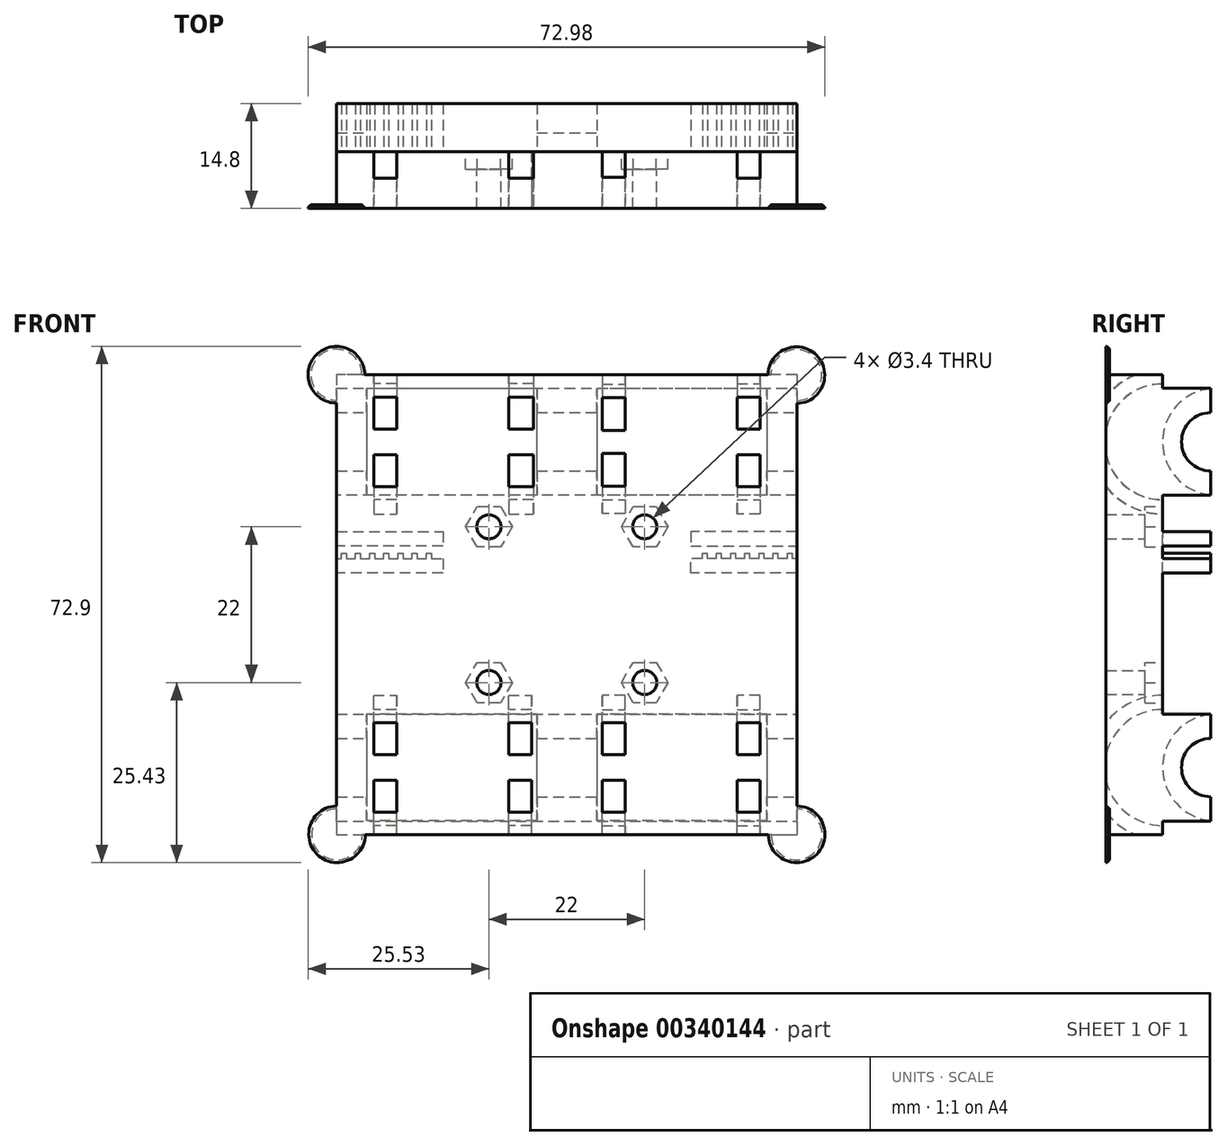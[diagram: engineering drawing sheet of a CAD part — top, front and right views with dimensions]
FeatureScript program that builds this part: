
annotation { "Feature Type Name" : "Feature", "Feature Type Description" : "" }
export const myFeature = defineFeature(function(context is Context, id is Id, definition is map)
    precondition{}
    {
        {
            var Q0;
            Q0=qCreatedBy(makeId("Front.planeOp"),FACE);
            var sketch = newSketch(context, id + "F0", { "sketchPlane" : qUnion([Q0])});
            skLineSegment(sketch, "E0", {"start": v(32.5, 32.5) * mm, "end": v(-32.5, 32.5) * mm});
            skLineSegment(sketch, "E1", {"start": v(-32.5, 32.5) * mm, "end": v(-32.5, -32.5) * mm});
            skLineSegment(sketch, "E2", {"start": v(-32.5, -32.5) * mm, "end": v(32.5, -32.5) * mm});
            skLineSegment(sketch, "E3", {"start": v(32.5, 32.5) * mm, "end": v(32.5, -32.5) * mm});
            skSolve(sketch);
        }
        {
            var Q0;
            Q0=makeQuery(id+"F0.imprint","IMPRINT",FACE,{"disambiguationData":[TD([[makeQuery(id+"F0.imprint","IMPRINT",EDGE,{"derivedFrom":sQuery(id+"F0.wireOp",EDGE,"E0")}),1.0]])]});
            extrude(context, id + "F1", {"entities" : qUnion([Q0]), "depth" : 8 * mm});
        }
        {
            var Q0;
            Q0=qCreatedBy(makeId("Front.planeOp"),FACE);
            var sketch = newSketch(context, id + "F2", { "sketchPlane" : qUnion([Q0])});
            skLineSegment(sketch, "E4", {"start": v(0, 0) * mm, "end": v(-11, 0) * mm});
            skLineSegment(sketch, "E5", {"start": v(-11, 0) * mm, "end": v(-11, 11) * mm});
            skLineSegment(sketch, "E6", {"start": v(-11, 11) * mm, "end": v(11, 11) * mm});
            skLineSegment(sketch, "E7", {"start": v(11, 11) * mm, "end": v(11, -11) * mm});
            skLineSegment(sketch, "E8", {"start": v(11, -11) * mm, "end": v(-11, -11) * mm});
            skCircle(sketch, "E9", {"center": v(-11, 11) * mm, "radius": 1.7 * mm});
            skCircle(sketch, "E10", {"center": v(11, 11) * mm, "radius": 1.7 * mm});
            skCircle(sketch, "E11", {"center": v(11, -11) * mm, "radius": 1.7 * mm});
            skCircle(sketch, "E12", {"center": v(-11, -11) * mm, "radius": 1.7 * mm});
            skSolve(sketch);
        }
        {
            var Q0;
            Q0=qSketchRegion(id+"F2",true);
            extrude(context, id + "F3", {"entities" : qUnion([Q0]), "operationType" : NewBodyOperationType.REMOVE, "depth" : 10 * mm});
        }
        {
            var Q0;
            Q0=qCreatedBy(makeId("Front.planeOp"),FACE);
            var sketch = newSketch(context, id + "F4", { "sketchPlane" : qUnion([Q0])});
            skLineSegment(sketch, "E13", {"start": v(0, 0) * mm, "end": v(11, 0) * mm});
            skLineSegment(sketch, "E14", {"start": v(-11, 11) * mm, "end": v(-11, -11) * mm});
            skLineSegment(sketch, "E15", {"start": v(-11, -11) * mm, "end": v(11, -11) * mm});
            skPoint(sketch, "E16", {"position": v(-11, 11) * mm});
            skPoint(sketch, "E17", {"position": v(-11, -11) * mm});
            skPoint(sketch, "E18", {"position": v(11, -11) * mm});
            skPoint(sketch, "E19", {"position": v(11, 11) * mm});
            skCircle(sketch, "E20.cCircle", {"center": v(-11, 11) * mm, "radius": 2.85 * mm, "construction": true});
            skLineSegment(sketch, "E20.0", {"start": v(-12.65, 13.85) * mm, "end": v(-9.35, 13.85) * mm});
            skLineSegment(sketch, "E20.1", {"start": v(-9.35, 13.85) * mm, "end": v(-7.7, 11) * mm});
            skLineSegment(sketch, "E20.2", {"start": v(-7.7, 11) * mm, "end": v(-9.35, 8.15) * mm});
            skLineSegment(sketch, "E20.3", {"start": v(-9.35, 8.15) * mm, "end": v(-12.65, 8.15) * mm});
            skLineSegment(sketch, "E20.4", {"start": v(-12.65, 8.15) * mm, "end": v(-14.3, 11) * mm});
            skLineSegment(sketch, "E20.5", {"start": v(-14.3, 11) * mm, "end": v(-12.65, 13.85) * mm});
            skPoint(sketch, "E20.0.midPoint", {"position": v(-11, 13.85) * mm});
            skCircle(sketch, "E21.cCircle", {"center": v(-11, -11) * mm, "radius": 2.85 * mm, "construction": true});
            skLineSegment(sketch, "E21.0", {"start": v(-12.65, -8.15) * mm, "end": v(-9.35, -8.15) * mm});
            skLineSegment(sketch, "E21.1", {"start": v(-9.35, -8.15) * mm, "end": v(-7.7, -11) * mm});
            skLineSegment(sketch, "E21.2", {"start": v(-7.7, -11) * mm, "end": v(-9.35, -13.85) * mm});
            skLineSegment(sketch, "E21.3", {"start": v(-9.35, -13.85) * mm, "end": v(-12.65, -13.85) * mm});
            skLineSegment(sketch, "E21.4", {"start": v(-12.65, -13.85) * mm, "end": v(-14.3, -11) * mm});
            skLineSegment(sketch, "E21.5", {"start": v(-14.3, -11) * mm, "end": v(-12.65, -8.15) * mm});
            skPoint(sketch, "E21.0.midPoint", {"position": v(-11, -8.15) * mm});
            skCircle(sketch, "E22.cCircle", {"center": v(11, -11) * mm, "radius": 2.85 * mm, "construction": true});
            skLineSegment(sketch, "E22.0", {"start": v(9.35, -8.15) * mm, "end": v(12.65, -8.15) * mm});
            skLineSegment(sketch, "E22.1", {"start": v(12.65, -8.15) * mm, "end": v(14.3, -11) * mm});
            skLineSegment(sketch, "E22.2", {"start": v(14.3, -11) * mm, "end": v(12.65, -13.85) * mm});
            skLineSegment(sketch, "E22.3", {"start": v(12.65, -13.85) * mm, "end": v(9.35, -13.85) * mm});
            skLineSegment(sketch, "E22.4", {"start": v(9.35, -13.85) * mm, "end": v(7.7, -11) * mm});
            skLineSegment(sketch, "E22.5", {"start": v(7.7, -11) * mm, "end": v(9.35, -8.15) * mm});
            skPoint(sketch, "E22.0.midPoint", {"position": v(11, -8.15) * mm});
            skCircle(sketch, "E23.cCircle", {"center": v(11, 11) * mm, "radius": 2.85 * mm, "construction": true});
            skLineSegment(sketch, "E23.0", {"start": v(9.35, 13.85) * mm, "end": v(12.65, 13.85) * mm});
            skLineSegment(sketch, "E23.1", {"start": v(12.65, 13.85) * mm, "end": v(14.3, 11) * mm});
            skLineSegment(sketch, "E23.2", {"start": v(14.3, 11) * mm, "end": v(12.65, 8.15) * mm});
            skLineSegment(sketch, "E23.3", {"start": v(12.65, 8.15) * mm, "end": v(9.35, 8.15) * mm});
            skLineSegment(sketch, "E23.4", {"start": v(9.35, 8.15) * mm, "end": v(7.7, 11) * mm});
            skLineSegment(sketch, "E23.5", {"start": v(7.7, 11) * mm, "end": v(9.35, 13.85) * mm});
            skPoint(sketch, "E23.0.midPoint", {"position": v(11, 13.85) * mm});
            skSolve(sketch);
        }
        {
            var Q0;
            Q0=qSketchRegion(id+"F4",true);
            extrude(context, id + "F5", {"entities" : qUnion([Q0]), "operationType" : NewBodyOperationType.REMOVE, "depth" : 2.5 * mm});
        }
        {
            var Q0;
            Q0=qCreatedBy(makeId("Right.planeOp"),FACE);
            var sketch = newSketch(context, id + "F6", { "sketchPlane" : qUnion([Q0])});
            skArc(sketch, "E24", {"start": v(7.55, 30.55) * mm, "mid": v(0, 23) * mm, "end": v(7.55, 15.45) * mm});
            skArc(sketch, "E25", {"start": v(7.55, -15.45) * mm, "mid": v(0, -23) * mm, "end": v(7.55, -30.55) * mm});
            skLineSegment(sketch, "E26", {"start": v(7.55, 30.55) * mm, "end": v(0, 30.55) * mm});
            skLineSegment(sketch, "E27", {"start": v(7.55, 15.45) * mm, "end": v(0, 15.45) * mm});
            skLineSegment(sketch, "E28", {"start": v(7.55, -15.45) * mm, "end": v(0, -15.45) * mm});
            skLineSegment(sketch, "E29", {"start": v(7.55, -30.55) * mm, "end": v(0, -30.55) * mm});
            skLineSegment(sketch, "E30", {"start": v(0, 15.45) * mm, "end": v(0, 30.55) * mm});
            skLineSegment(sketch, "E31", {"start": v(0, -15.45) * mm, "end": v(0, -30.55) * mm});
            skSolve(sketch);
        }
        {
            var Q0;
            Q0=qSketchRegion(id+"F6",true);
            extrude(context, id + "F7", {"entities" : qUnion([Q0]), "operationType" : NewBodyOperationType.ADD, "endBound" : BoundingType.SYMMETRIC, "depth" : 65 * mm});
        }
        {
            var Q0;
            Q0=qCreatedBy(makeId("Front.planeOp"),FACE);
            var sketch = newSketch(context, id + "F8", { "sketchPlane" : qUnion([Q0])});
            skLineSegment(sketch, "E32", {"start": v(-4.23, 30.55) * mm, "end": v(-4.23, 15.45) * mm});
            skLineSegment(sketch, "E33", {"start": v(-4.23, 15.45) * mm, "end": v(4.22, 15.45) * mm});
            skLineSegment(sketch, "E34", {"start": v(4.22, 15.45) * mm, "end": v(4.22, 30.55) * mm});
            skLineSegment(sketch, "E35", {"start": v(4.22, 30.55) * mm, "end": v(-4.23, 30.55) * mm});
            skLineSegment(sketch, "E36", {"start": v(28.28, 15.45) * mm, "end": v(28.28, 30.55) * mm});
            skLineSegment(sketch, "E37", {"start": v(-28.28, 15.45) * mm, "end": v(-28.28, 30.55) * mm});
            skLineSegment(sketch, "E38", {"start": v(28.28, 15.45) * mm, "end": v(32.5, 15.45) * mm});
            skLineSegment(sketch, "E39", {"start": v(32.5, 15.45) * mm, "end": v(32.5, 30.55) * mm});
            skLineSegment(sketch, "E40", {"start": v(32.5, 30.55) * mm, "end": v(28.28, 30.55) * mm});
            skLineSegment(sketch, "E41", {"start": v(-28.28, 15.45) * mm, "end": v(-32.5, 15.45) * mm});
            skLineSegment(sketch, "E42", {"start": v(-32.5, 15.45) * mm, "end": v(-32.5, 30.55) * mm});
            skLineSegment(sketch, "E43", {"start": v(-32.5, 30.55) * mm, "end": v(-28.28, 30.55) * mm});
            skLineSegment(sketch, "E44", {"start": v(0, 0) * mm, "end": v(0, -15.45) * mm});
            skLineSegment(sketch, "E45", {"start": v(-4.22, -15.45) * mm, "end": v(-4.22, -30.55) * mm});
            skLineSegment(sketch, "E46", {"start": v(-4.22, -30.55) * mm, "end": v(4.23, -30.55) * mm});
            skLineSegment(sketch, "E47", {"start": v(4.23, -30.55) * mm, "end": v(4.23, -15.45) * mm});
            skLineSegment(sketch, "E48", {"start": v(4.23, -15.45) * mm, "end": v(-4.22, -15.45) * mm});
            skLineSegment(sketch, "E49", {"start": v(-32.5, -15.45) * mm, "end": v(-32.5, -30.55) * mm});
            skLineSegment(sketch, "E50", {"start": v(-32.5, -30.55) * mm, "end": v(-28.28, -30.55) * mm});
            skLineSegment(sketch, "E51", {"start": v(-28.28, -30.55) * mm, "end": v(-28.28, -15.45) * mm});
            skLineSegment(sketch, "E52", {"start": v(-28.28, -15.45) * mm, "end": v(-32.5, -15.45) * mm});
            skLineSegment(sketch, "E53", {"start": v(32.5, -15.45) * mm, "end": v(32.5, -30.55) * mm});
            skLineSegment(sketch, "E54", {"start": v(32.5, -30.55) * mm, "end": v(28.28, -30.55) * mm});
            skLineSegment(sketch, "E55", {"start": v(28.28, -30.55) * mm, "end": v(28.28, -15.45) * mm});
            skLineSegment(sketch, "E56", {"start": v(28.28, -15.45) * mm, "end": v(32.5, -15.45) * mm});
            skSolve(sketch);
        }
        {
            var Q0;
            Q0=qSketchRegion(id+"F8",true);
            extrude(context, id + "F9", {"entities" : qUnion([Q0]), "operationType" : NewBodyOperationType.ADD, "oppositeDirection" : true, "depth" : 7.55 * mm});
        }
        {
            var Q0;
            Q0=qCreatedBy(makeId("Right.planeOp"),FACE);
            var sketch = newSketch(context, id + "F10", { "sketchPlane" : qUnion([Q0])});
            skLineSegment(sketch, "E57", {"start": v(6.8, 23) * mm, "end": v(6.8, 31.2) * mm});
            skLineSegment(sketch, "E58", {"start": v(6.8, 31.2) * mm, "end": v(8.17, 31.2) * mm});
            skLineSegment(sketch, "E59", {"start": v(8.17, 31.2) * mm, "end": v(8.17, 14.58) * mm});
            skLineSegment(sketch, "E60", {"start": v(8.17, 14.58) * mm, "end": v(6.8, 14.58) * mm});
            skLineSegment(sketch, "E61", {"start": v(6.8, 14.58) * mm, "end": v(6.8, 23) * mm});
            skLineSegment(sketch, "E62", {"start": v(6.8, -23) * mm, "end": v(6.8, -14.35) * mm});
            skLineSegment(sketch, "E63", {"start": v(6.8, -14.35) * mm, "end": v(8.14, -14.35) * mm});
            skLineSegment(sketch, "E64", {"start": v(8.14, -14.35) * mm, "end": v(8.14, -31.51) * mm});
            skLineSegment(sketch, "E65", {"start": v(8.14, -31.51) * mm, "end": v(6.8, -31.51) * mm});
            skLineSegment(sketch, "E66", {"start": v(6.8, -31.51) * mm, "end": v(6.8, -23) * mm});
            skLineSegment(sketch, "E67", {"start": v(0, 0) * mm, "end": v(0, 23) * mm});
            skLineSegment(sketch, "E68", {"start": v(0, 23) * mm, "end": v(6.8, 23) * mm});
            skLineSegment(sketch, "E69", {"start": v(0, 0) * mm, "end": v(0, -23) * mm});
            skLineSegment(sketch, "E70", {"start": v(0, -23) * mm, "end": v(6.8, -23) * mm});
            skSolve(sketch);
        }
        {
            var Q0;
            Q0=qSketchRegion(id+"F10",true);
            extrude(context, id + "F11", {"entities" : qUnion([Q0]), "operationType" : NewBodyOperationType.REMOVE, "endBound" : BoundingType.SYMMETRIC, "oppositeDirection" : true, "depth" : 70 * mm});
        }
        {
            var Q0;
            Q0=makeQuery(id+"F1.opExtrude","SWEPT_BODY",BODY,{"disambiguationData":[OSD([sQuery(id+"F0.wireOp",EDGE,"E0"),sQuery(id+"F0.wireOp",EDGE,"E1"),sQuery(id+"F0.wireOp",EDGE,"E2"),sQuery(id+"F0.wireOp",EDGE,"E3")])]});
            transform(context, id + "F12", {"entities" : qUnion([Q0]), "transformType" : TransformType.TRANSLATION_3D, "dx" : 5.22 * mm, "dy" : 0 * mm, "dz" : -23 * mm, "makeCopy" : false});
        }
        {
            var Q0;
            Q0=qCreatedBy(makeId("Front.planeOp"),FACE);
            var sketch = newSketch(context, id + "F13", { "sketchPlane" : qUnion([Q0])});
            skLineSegment(sketch, "E71", {"start": v(0.5, 8.2) * mm, "end": v(-3, 8.2) * mm});
            skLineSegment(sketch, "E72", {"start": v(-3, 8.2) * mm, "end": v(-3, 10.2) * mm});
            skLineSegment(sketch, "E73", {"start": v(-3, 10.2) * mm, "end": v(0.5, 10.2) * mm});
            skLineSegment(sketch, "E74", {"start": v(0.5, 10.2) * mm, "end": v(0.5, 8.2) * mm});
            skSolve(sketch);
        }
        {
            var Q0;
            Q0=qCreatedBy(makeId("Right.planeOp"),FACE);
            var sketch = newSketch(context, id + "F14", { "sketchPlane" : qUnion([Q0])});
            skArc(sketch, "E75", {"start": v(0, 9.5) * mm, "mid": v(-9.5, 0) * mm, "end": v(0, -9.5) * mm});
            skSolve(sketch);
        }
        {
            var Q0;
            Q0=qSketchRegion(id+"F13",true);
            var Q1;
            Q1=qConstructionFilter(qBodyType(qCreatedBy(id+"F14",EDGE),BodyType.WIRE),ConstructionObject.NO);
            sweep(context, id + "F15", {"operationType" : NewBodyOperationType.REMOVE, "profiles" : qUnion([Q0]), "path" : qUnion([Q1])});
        }
        {
            var Q0;
            Q0=makeQuery(id+"F1.opExtrude","SWEPT_BODY",BODY,{"disambiguationData":[OSD([sQuery(id+"F0.wireOp",EDGE,"E0"),sQuery(id+"F0.wireOp",EDGE,"E1"),sQuery(id+"F0.wireOp",EDGE,"E2"),sQuery(id+"F0.wireOp",EDGE,"E3")])]});
            transform(context, id + "F16", {"entities" : qUnion([Q0]), "transformType" : TransformType.TRANSLATION_3D, "dx" : 19.05 * mm, "dy" : 0 * mm, "dz" : 0 * mm, "makeCopy" : false});
        }
        {
            var Q0;
            Q0=qCreatedBy(makeId("Front.planeOp"),FACE);
            var sketch = newSketch(context, id + "F17", { "sketchPlane" : qUnion([Q0])});
            skLineSegment(sketch, "E76", {"start": v(0.25, 8.2) * mm, "end": v(-3, 8.2) * mm});
            skLineSegment(sketch, "E77", {"start": v(-3, 8.2) * mm, "end": v(-3, 10.2) * mm});
            skLineSegment(sketch, "E78", {"start": v(-3, 10.2) * mm, "end": v(0.25, 10.2) * mm});
            skLineSegment(sketch, "E79", {"start": v(0.25, 10.2) * mm, "end": v(0.25, 8.2) * mm});
            skSolve(sketch);
        }
        {
            var Q0;
            Q0=qSketchRegion(id+"F17",true);
            var Q1;
            Q1=qConstructionFilter(qBodyType(qCreatedBy(id+"F14",EDGE),BodyType.WIRE),ConstructionObject.NO);
            sweep(context, id + "F18", {"operationType" : NewBodyOperationType.REMOVE, "profiles" : qUnion([Q0]), "path" : qUnion([Q1])});
        }
        {
            var Q0;
            Q0=makeQuery(id+"F1.opExtrude","SWEPT_BODY",BODY,{"disambiguationData":[OSD([sQuery(id+"F0.wireOp",EDGE,"E0"),sQuery(id+"F0.wireOp",EDGE,"E1"),sQuery(id+"F0.wireOp",EDGE,"E2"),sQuery(id+"F0.wireOp",EDGE,"E3")])]});
            transform(context, id + "F19", {"entities" : qUnion([Q0]), "transformType" : TransformType.TRANSLATION_3D, "dx" : -24.27 * mm, "dy" : 0 * mm, "dz" : 0 * mm, "makeCopy" : false});
        }
        {
            var Q0;
            Q0=makeQuery(id+"F1.opExtrude","SWEPT_BODY",BODY,{"disambiguationData":[OSD([sQuery(id+"F0.wireOp",EDGE,"E0"),sQuery(id+"F0.wireOp",EDGE,"E1"),sQuery(id+"F0.wireOp",EDGE,"E2"),sQuery(id+"F0.wireOp",EDGE,"E3")])]});
            transform(context, id + "F20", {"entities" : qUnion([Q0]), "transformType" : TransformType.TRANSLATION_3D, "dx" : -5.22 * mm, "dy" : 0 * mm, "dz" : 0 * mm, "makeCopy" : false});
        }
        {
            var Q0;
            Q0=qCreatedBy(makeId("Front.planeOp"),FACE);
            var sketch = newSketch(context, id + "F21", { "sketchPlane" : qUnion([Q0])});
            skLineSegment(sketch, "E80", {"start": v(-0.25, 8.16) * mm, "end": v(3, 8.16) * mm});
            skLineSegment(sketch, "E81", {"start": v(3, 8.16) * mm, "end": v(3, 10.16) * mm});
            skLineSegment(sketch, "E82", {"start": v(3, 10.16) * mm, "end": v(-0.25, 10.16) * mm});
            skLineSegment(sketch, "E83", {"start": v(-0.25, 10.16) * mm, "end": v(-0.25, 8.16) * mm});
            skSolve(sketch);
        }
        {
            var Q0;
            Q0=qSketchRegion(id+"F21",true);
            var Q1;
            Q1=qConstructionFilter(qBodyType(qCreatedBy(id+"F14",EDGE),BodyType.WIRE),ConstructionObject.NO);
            sweep(context, id + "F22", {"operationType" : NewBodyOperationType.REMOVE, "profiles" : qUnion([Q0]), "path" : qUnion([Q1])});
        }
        {
            var Q0;
            Q0=makeQuery(id+"F1.opExtrude","SWEPT_BODY",BODY,{"disambiguationData":[OSD([sQuery(id+"F0.wireOp",EDGE,"E0"),sQuery(id+"F0.wireOp",EDGE,"E1"),sQuery(id+"F0.wireOp",EDGE,"E2"),sQuery(id+"F0.wireOp",EDGE,"E3")])]});
            transform(context, id + "F23", {"entities" : qUnion([Q0]), "transformType" : TransformType.TRANSLATION_3D, "dx" : -19.05 * mm, "dy" : 0 * mm, "dz" : 0 * mm, "makeCopy" : false});
        }
        {
            var Q0;
            Q0=qCreatedBy(makeId("Front.planeOp"),FACE);
            var sketch = newSketch(context, id + "F24", { "sketchPlane" : qUnion([Q0])});
            skLineSegment(sketch, "E84", {"start": v(-0.25, 8.2) * mm, "end": v(3, 8.2) * mm});
            skLineSegment(sketch, "E85", {"start": v(3, 8.2) * mm, "end": v(3, 10.2) * mm});
            skLineSegment(sketch, "E86", {"start": v(3, 10.2) * mm, "end": v(-0.25, 10.2) * mm});
            skLineSegment(sketch, "E87", {"start": v(-0.25, 10.2) * mm, "end": v(-0.25, 8.2) * mm});
            skSolve(sketch);
        }
        {
            var Q0;
            Q0=qSketchRegion(id+"F24",true);
            var Q1;
            Q1=sQuery(id+"F14.wireOp",EDGE,"E75");
            sweep(context, id + "F25", {"operationType" : NewBodyOperationType.REMOVE, "profiles" : qUnion([Q0]), "path" : qUnion([Q1])});
        }
        {
            var Q0;
            Q0=makeQuery(id+"F1.opExtrude","SWEPT_BODY",BODY,{"disambiguationData":[OSD([sQuery(id+"F0.wireOp",EDGE,"E0"),sQuery(id+"F0.wireOp",EDGE,"E1"),sQuery(id+"F0.wireOp",EDGE,"E2"),sQuery(id+"F0.wireOp",EDGE,"E3")])]});
            transform(context, id + "F26", {"entities" : qUnion([Q0]), "transformType" : TransformType.TRANSLATION_3D, "dx" : 0 * mm, "dy" : 0 * mm, "dz" : 46 * mm, "makeCopy" : false});
        }
        {
            var Q0;
            Q0=qCreatedBy(makeId("Front.planeOp"),FACE);
            var sketch = newSketch(context, id + "F27", { "sketchPlane" : qUnion([Q0])});
            skLineSegment(sketch, "E88", {"start": v(-0.25, -8.2) * mm, "end": v(3, -8.2) * mm});
            skLineSegment(sketch, "E89", {"start": v(3, -8.2) * mm, "end": v(3, -10.2) * mm});
            skLineSegment(sketch, "E90", {"start": v(3, -10.2) * mm, "end": v(-0.25, -10.2) * mm});
            skLineSegment(sketch, "E91", {"start": v(-0.25, -10.2) * mm, "end": v(-0.25, -8.2) * mm});
            skSolve(sketch);
        }
        {
            var Q0;
            Q0=qSketchRegion(id+"F27",true);
            var Q1;
            Q1=sQuery(id+"F14.wireOp",EDGE,"E75");
            sweep(context, id + "F28", {"operationType" : NewBodyOperationType.REMOVE, "profiles" : qUnion([Q0]), "path" : qUnion([Q1])});
        }
        {
            var Q0;
            Q0=makeQuery(id+"F1.opExtrude","SWEPT_BODY",BODY,{"disambiguationData":[OSD([sQuery(id+"F0.wireOp",EDGE,"E0"),sQuery(id+"F0.wireOp",EDGE,"E1"),sQuery(id+"F0.wireOp",EDGE,"E2"),sQuery(id+"F0.wireOp",EDGE,"E3")])]});
            transform(context, id + "F29", {"entities" : qUnion([Q0]), "transformType" : TransformType.TRANSLATION_3D, "dx" : 19.05 * mm, "dy" : 0 * mm, "dz" : 0 * mm, "makeCopy" : false});
        }
        {
            var Q0;
            Q0=qCreatedBy(makeId("Front.planeOp"),FACE);
            var sketch = newSketch(context, id + "F30", { "sketchPlane" : qUnion([Q0])});
            skLineSegment(sketch, "E92", {"start": v(-0.25, -8.2) * mm, "end": v(3, -8.2) * mm});
            skLineSegment(sketch, "E93", {"start": v(3, -8.2) * mm, "end": v(3, -10.2) * mm});
            skLineSegment(sketch, "E94", {"start": v(3, -10.2) * mm, "end": v(-0.25, -10.2) * mm});
            skLineSegment(sketch, "E95", {"start": v(-0.25, -10.2) * mm, "end": v(-0.25, -8.2) * mm});
            skSolve(sketch);
        }
        {
            var Q0;
            Q0=qSketchRegion(id+"F30",true);
            var Q1;
            Q1=qConstructionFilter(qBodyType(qCreatedBy(id+"F14",EDGE),BodyType.WIRE),ConstructionObject.NO);
            sweep(context, id + "F31", {"operationType" : NewBodyOperationType.REMOVE, "profiles" : qUnion([Q0]), "path" : qUnion([Q1])});
        }
        {
            var Q0;
            Q0=makeQuery(id+"F1.opExtrude","SWEPT_BODY",BODY,{"disambiguationData":[OSD([sQuery(id+"F0.wireOp",EDGE,"E0"),sQuery(id+"F0.wireOp",EDGE,"E1"),sQuery(id+"F0.wireOp",EDGE,"E2"),sQuery(id+"F0.wireOp",EDGE,"E3")])]});
            transform(context, id + "F32", {"entities" : qUnion([Q0]), "transformType" : TransformType.TRANSLATION_3D, "dx" : 10.45 * mm, "dy" : 0 * mm, "dz" : 0 * mm, "makeCopy" : false});
        }
        {
            var Q0;
            Q0=qCreatedBy(makeId("Front.planeOp"),FACE);
            var sketch = newSketch(context, id + "F33", { "sketchPlane" : qUnion([Q0])});
            skLineSegment(sketch, "E96", {"start": v(0.25, -8.2) * mm, "end": v(-3, -8.2) * mm});
            skLineSegment(sketch, "E97", {"start": v(-3, -8.2) * mm, "end": v(-3, -10.2) * mm});
            skLineSegment(sketch, "E98", {"start": v(-3, -10.2) * mm, "end": v(0.25, -10.2) * mm});
            skLineSegment(sketch, "E99", {"start": v(0.25, -10.2) * mm, "end": v(0.25, -8.2) * mm});
            skSolve(sketch);
        }
        {
            var Q0;
            Q0=qSketchRegion(id+"F33",true);
            var Q1;
            Q1=qConstructionFilter(qBodyType(qCreatedBy(id+"F14",EDGE),BodyType.WIRE),ConstructionObject.NO);
            sweep(context, id + "F34", {"operationType" : NewBodyOperationType.REMOVE, "profiles" : qUnion([Q0]), "path" : qUnion([Q1])});
        }
        {
            var Q0;
            Q0=makeQuery(id+"F1.opExtrude","SWEPT_BODY",BODY,{"disambiguationData":[OSD([sQuery(id+"F0.wireOp",EDGE,"E0"),sQuery(id+"F0.wireOp",EDGE,"E1"),sQuery(id+"F0.wireOp",EDGE,"E2"),sQuery(id+"F0.wireOp",EDGE,"E3")])]});
            transform(context, id + "F35", {"entities" : qUnion([Q0]), "transformType" : TransformType.TRANSLATION_3D, "dx" : 19.05 * mm, "dy" : 0 * mm, "dz" : 0 * mm, "makeCopy" : false});
        }
        {
            var Q0;
            Q0=qCreatedBy(makeId("Front.planeOp"),FACE);
            var sketch = newSketch(context, id + "F36", { "sketchPlane" : qUnion([Q0])});
            skLineSegment(sketch, "E100", {"start": v(0.25, -8.2) * mm, "end": v(-3, -8.2) * mm});
            skLineSegment(sketch, "E101", {"start": v(-3, -8.2) * mm, "end": v(-3, -10.2) * mm});
            skLineSegment(sketch, "E102", {"start": v(-3, -10.2) * mm, "end": v(0.25, -10.2) * mm});
            skLineSegment(sketch, "E103", {"start": v(0.25, -10.2) * mm, "end": v(0.25, -8.2) * mm});
            skSolve(sketch);
        }
        {
            var Q0;
            Q0=qSketchRegion(id+"F36",true);
            var Q1;
            Q1=qConstructionFilter(qBodyType(qCreatedBy(id+"F14",EDGE),BodyType.WIRE),ConstructionObject.NO);
            sweep(context, id + "F37", {"operationType" : NewBodyOperationType.REMOVE, "profiles" : qUnion([Q0]), "path" : qUnion([Q1])});
        }
        {
            var Q0;
            Q0=makeQuery(id+"F1.opExtrude","SWEPT_BODY",BODY,{"disambiguationData":[OSD([sQuery(id+"F0.wireOp",EDGE,"E0"),sQuery(id+"F0.wireOp",EDGE,"E1"),sQuery(id+"F0.wireOp",EDGE,"E2"),sQuery(id+"F0.wireOp",EDGE,"E3")])]});
            transform(context, id + "F38", {"entities" : qUnion([Q0]), "transformType" : TransformType.TRANSLATION_3D, "dx" : -24.27 * mm, "dy" : 0 * mm, "dz" : -23 * mm, "makeCopy" : false});
        }
        {
            var Q0;
            Q0=qCreatedBy(makeId("Front.planeOp"),FACE);
            var sketch = newSketch(context, id + "F39", { "sketchPlane" : qUnion([Q0])});
            skPoint(sketch, "E104", {"position": v(32.5, 10.3) * mm});
            skLineSegment(sketch, "E105", {"start": v(32.5, 10.3) * mm, "end": v(17.5, 10.3) * mm});
            skLineSegment(sketch, "E106", {"start": v(17.5, 10.3) * mm, "end": v(17.5, 8.3) * mm});
            skLineSegment(sketch, "E107", {"start": v(17.5, 8.3) * mm, "end": v(32.5, 8.3) * mm});
            skLineSegment(sketch, "E108", {"start": v(32.5, 8.3) * mm, "end": v(32.5, 10.3) * mm});
            skPoint(sketch, "E109", {"position": v(32.5, 6.5) * mm});
            skLineSegment(sketch, "E110", {"start": v(32.5, 6.5) * mm, "end": v(31.85, 6.5) * mm});
            skLineSegment(sketch, "E111", {"start": v(31.85, 6.5) * mm, "end": v(31.85, 7.25) * mm});
            skLineSegment(sketch, "E112", {"start": v(31.15, 6.5) * mm, "end": v(31.15, 7.25) * mm});
            skLineSegment(sketch, "E113", {"start": v(29.85, 6.5) * mm, "end": v(29.85, 7.25) * mm});
            skLineSegment(sketch, "E114", {"start": v(29.15, 6.5) * mm, "end": v(29.15, 7.25) * mm});
            skLineSegment(sketch, "E115", {"start": v(27.85, 6.5) * mm, "end": v(27.85, 7.25) * mm});
            skLineSegment(sketch, "E116", {"start": v(27.15, 6.5) * mm, "end": v(27.15, 7.25) * mm});
            skLineSegment(sketch, "E117", {"start": v(25.85, 6.5) * mm, "end": v(25.85, 7.25) * mm});
            skLineSegment(sketch, "E118", {"start": v(25.15, 6.5) * mm, "end": v(25.15, 7.25) * mm});
            skLineSegment(sketch, "E119", {"start": v(23.85, 6.5) * mm, "end": v(23.85, 7.25) * mm});
            skLineSegment(sketch, "E120", {"start": v(23.15, 6.5) * mm, "end": v(23.15, 7.25) * mm});
            skLineSegment(sketch, "E121", {"start": v(21.85, 6.5) * mm, "end": v(21.85, 7.25) * mm});
            skLineSegment(sketch, "E122", {"start": v(21.15, 6.5) * mm, "end": v(21.15, 7.25) * mm});
            skLineSegment(sketch, "E123", {"start": v(19.85, 6.5) * mm, "end": v(19.85, 7.25) * mm});
            skLineSegment(sketch, "E124", {"start": v(19.15, 6.5) * mm, "end": v(19.15, 7.25) * mm});
            skLineSegment(sketch, "E125", {"start": v(32.5, 6.5) * mm, "end": v(32.5, 4.5) * mm});
            skLineSegment(sketch, "E126", {"start": v(32.5, 4.5) * mm, "end": v(17.5, 4.5) * mm});
            skLineSegment(sketch, "E127", {"start": v(17.5, 4.5) * mm, "end": v(17.5, 6.5) * mm});
            skLineSegment(sketch, "E128", {"start": v(19.15, 7.25) * mm, "end": v(19.85, 7.25) * mm});
            skLineSegment(sketch, "E129", {"start": v(21.15, 7.25) * mm, "end": v(21.85, 7.25) * mm});
            skLineSegment(sketch, "E130", {"start": v(23.15, 7.25) * mm, "end": v(23.85, 7.25) * mm});
            skLineSegment(sketch, "E131", {"start": v(25.15, 7.25) * mm, "end": v(25.85, 7.25) * mm});
            skLineSegment(sketch, "E132", {"start": v(27.15, 7.25) * mm, "end": v(27.85, 7.25) * mm});
            skLineSegment(sketch, "E133", {"start": v(29.15, 7.25) * mm, "end": v(29.85, 7.25) * mm});
            skLineSegment(sketch, "E134", {"start": v(31.15, 7.25) * mm, "end": v(31.85, 7.25) * mm});
            skLineSegment(sketch, "E135", {"start": v(19.15, 6.5) * mm, "end": v(17.5, 6.5) * mm});
            skLineSegment(sketch, "E136", {"start": v(31.15, 6.5) * mm, "end": v(29.85, 6.5) * mm});
            skLineSegment(sketch, "E137", {"start": v(29.15, 6.5) * mm, "end": v(27.85, 6.5) * mm});
            skLineSegment(sketch, "E138", {"start": v(27.15, 6.5) * mm, "end": v(25.85, 6.5) * mm});
            skLineSegment(sketch, "E139", {"start": v(25.15, 6.5) * mm, "end": v(23.85, 6.5) * mm});
            skLineSegment(sketch, "E140", {"start": v(23.15, 6.5) * mm, "end": v(21.85, 6.5) * mm});
            skLineSegment(sketch, "E141", {"start": v(21.15, 6.5) * mm, "end": v(19.85, 6.5) * mm});
            skLineSegment(sketch, "E142", {"start": v(-17.5, 8.3) * mm, "end": v(-32.5, 8.3) * mm});
            skLineSegment(sketch, "E143", {"start": v(-32.5, 8.3) * mm, "end": v(-32.5, 10.3) * mm});
            skLineSegment(sketch, "E144", {"start": v(-32.5, 10.3) * mm, "end": v(-17.5, 10.3) * mm});
            skLineSegment(sketch, "E145", {"start": v(-17.5, 10.3) * mm, "end": v(-17.5, 8.3) * mm});
            skLineSegment(sketch, "E146", {"start": v(-32.5, 8.3) * mm, "end": v(-32.5, 6.5) * mm});
            skLineSegment(sketch, "E147", {"start": v(-32.5, 6.5) * mm, "end": v(-31.85, 6.5) * mm});
            skLineSegment(sketch, "E148", {"start": v(-31.85, 6.5) * mm, "end": v(-31.85, 7.25) * mm});
            skLineSegment(sketch, "E149", {"start": v(-31.85, 7.25) * mm, "end": v(-31.15, 7.25) * mm});
            skLineSegment(sketch, "E150", {"start": v(-31.15, 7.25) * mm, "end": v(-31.15, 6.5) * mm});
            skLineSegment(sketch, "E151", {"start": v(-31.15, 6.5) * mm, "end": v(-29.85, 6.5) * mm});
            skLineSegment(sketch, "E152", {"start": v(-29.85, 6.5) * mm, "end": v(-29.85, 7.25) * mm});
            skLineSegment(sketch, "E153", {"start": v(-29.85, 7.25) * mm, "end": v(-29.15, 7.25) * mm});
            skLineSegment(sketch, "E154", {"start": v(-29.15, 7.25) * mm, "end": v(-29.15, 6.5) * mm});
            skLineSegment(sketch, "E155", {"start": v(-29.15, 6.5) * mm, "end": v(-27.85, 6.5) * mm});
            skLineSegment(sketch, "E156", {"start": v(-27.85, 6.5) * mm, "end": v(-27.85, 7.25) * mm});
            skLineSegment(sketch, "E157", {"start": v(-27.85, 7.25) * mm, "end": v(-27.15, 7.25) * mm});
            skLineSegment(sketch, "E158", {"start": v(-27.15, 7.25) * mm, "end": v(-27.15, 6.5) * mm});
            skLineSegment(sketch, "E159", {"start": v(-27.15, 6.5) * mm, "end": v(-25.85, 6.5) * mm});
            skLineSegment(sketch, "E160", {"start": v(-25.85, 6.5) * mm, "end": v(-25.85, 7.25) * mm});
            skLineSegment(sketch, "E161", {"start": v(-25.85, 7.25) * mm, "end": v(-25.15, 7.25) * mm});
            skLineSegment(sketch, "E162", {"start": v(-25.15, 7.25) * mm, "end": v(-25.15, 6.5) * mm});
            skLineSegment(sketch, "E163", {"start": v(-25.15, 6.5) * mm, "end": v(-23.85, 6.5) * mm});
            skLineSegment(sketch, "E164", {"start": v(-23.85, 6.5) * mm, "end": v(-23.85, 7.25) * mm});
            skLineSegment(sketch, "E165", {"start": v(-23.85, 7.25) * mm, "end": v(-23.15, 7.25) * mm});
            skLineSegment(sketch, "E166", {"start": v(-23.15, 7.25) * mm, "end": v(-23.15, 6.5) * mm});
            skLineSegment(sketch, "E167", {"start": v(-23.15, 6.5) * mm, "end": v(-21.85, 6.5) * mm});
            skLineSegment(sketch, "E168", {"start": v(-21.85, 6.5) * mm, "end": v(-21.85, 7.25) * mm});
            skLineSegment(sketch, "E169", {"start": v(-21.85, 7.25) * mm, "end": v(-21.15, 7.25) * mm});
            skLineSegment(sketch, "E170", {"start": v(-21.15, 7.25) * mm, "end": v(-21.15, 6.5) * mm});
            skLineSegment(sketch, "E171", {"start": v(-21.15, 6.5) * mm, "end": v(-19.85, 6.5) * mm});
            skLineSegment(sketch, "E172", {"start": v(-19.85, 6.5) * mm, "end": v(-19.85, 7.25) * mm});
            skLineSegment(sketch, "E173", {"start": v(-19.85, 7.25) * mm, "end": v(-19.15, 7.25) * mm});
            skLineSegment(sketch, "E174", {"start": v(-19.15, 7.25) * mm, "end": v(-19.15, 6.5) * mm});
            skLineSegment(sketch, "E175", {"start": v(-19.15, 6.5) * mm, "end": v(-17.5, 6.5) * mm});
            skLineSegment(sketch, "E176", {"start": v(-17.5, 6.5) * mm, "end": v(-17.5, 4.5) * mm});
            skLineSegment(sketch, "E177", {"start": v(-17.5, 4.5) * mm, "end": v(-32.5, 4.5) * mm});
            skLineSegment(sketch, "E178", {"start": v(-32.5, 4.5) * mm, "end": v(-32.5, 6.5) * mm});
            skSolve(sketch);
        }
        {
            var Q0;
            Q0=qSketchRegion(id+"F39",true);
            extrude(context, id + "F40", {"entities" : qUnion([Q0]), "operationType" : NewBodyOperationType.ADD, "oppositeDirection" : true, "depth" : 6.8 * mm});
        }
        {
            var Q0;
            Q0=qCreatedBy(makeId("Right.planeOp"),FACE);
            var sketch = newSketch(context, id + "F41", { "sketchPlane" : qUnion([Q0])});
            skCircle(sketch, "E179", {"center": v(6.8, 23) * mm, "radius": 4.12 * mm});
            skLineSegment(sketch, "E180", {"start": v(0, 0) * mm, "end": v(0, -23) * mm});
            skLineSegment(sketch, "E181", {"start": v(0, -23) * mm, "end": v(6.8, -23) * mm});
            skCircle(sketch, "E182", {"center": v(6.8, -23) * mm, "radius": 4.12 * mm});
            skSolve(sketch);
        }
        {
            var Q0;
            Q0=qSketchRegion(id+"F41",true);
            extrude(context, id + "F42", {"entities" : qUnion([Q0]), "operationType" : NewBodyOperationType.REMOVE, "endBound" : BoundingType.SYMMETRIC, "oppositeDirection" : true, "depth" : 70 * mm});
        }
        {
            var Q0;
            Q0=makeQuery(id+"F1.opExtrude","SWEPT_BODY",BODY,{"disambiguationData":[OSD([sQuery(id+"F0.wireOp",EDGE,"E0"),sQuery(id+"F0.wireOp",EDGE,"E1"),sQuery(id+"F0.wireOp",EDGE,"E2"),sQuery(id+"F0.wireOp",EDGE,"E3")])]});
            transform(context, id + "F43", {"entities" : qUnion([Q0]), "transformType" : TransformType.TRANSLATION_3D, "dx" : 0 * mm, "dy" : 8 * mm, "dz" : 0 * mm, "makeCopy" : false});
        }
        {
            var Q0;
            Q0=qCreatedBy(makeId("Front.planeOp"),FACE);
            var sketch = newSketch(context, id + "F44", { "sketchPlane" : qUnion([Q0])});
            skCircle(sketch, "E183", {"center": v(32.42, 32.42) * mm, "radius": 4 * mm});
            skCircle(sketch, "E184", {"center": v(-32.53, 32.47) * mm, "radius": 4 * mm});
            skCircle(sketch, "E185", {"center": v(-32.45, -32.43) * mm, "radius": 4 * mm});
            skCircle(sketch, "E186", {"center": v(32.45, -32.43) * mm, "radius": 4 * mm});
            skSolve(sketch);
        }
        {
            var Q0;
            Q0=qSketchRegion(id+"F44",true);
            extrude(context, id + "F45", {"entities" : qUnion([Q0]), "operationType" : NewBodyOperationType.ADD, "oppositeDirection" : true, "depth" : .5 * mm});
        }
        {
            var Q0;
            Q0=makeQuery(id+"F45.opExtrude","CAP_EDGE",EDGE,{"disambiguationData":[OSD([sQuery(id+"F44.wireOp",EDGE,"E183")])],"isStart":false});
            var Q1;
            Q1=makeQuery(id+"F45.opExtrude","CAP_EDGE",EDGE,{"disambiguationData":[OSD([sQuery(id+"F44.wireOp",EDGE,"E184")])],"isStart":false});
            var Q2;
            Q2=makeQuery(id+"F45.opExtrude","CAP_EDGE",EDGE,{"disambiguationData":[OSD([sQuery(id+"F44.wireOp",EDGE,"E186")])],"isStart":false});
            var Q3;
            Q3=makeQuery(id+"F45.opExtrude","CAP_EDGE",EDGE,{"disambiguationData":[OSD([sQuery(id+"F44.wireOp",EDGE,"E185")])],"isStart":false});
            chamfer(context, id + "F46", {"entities" : qUnion([Q0, Q1, Q2, Q3]), "width" : .4 * mm, "tangentPropagation" : true});
        }
    });
